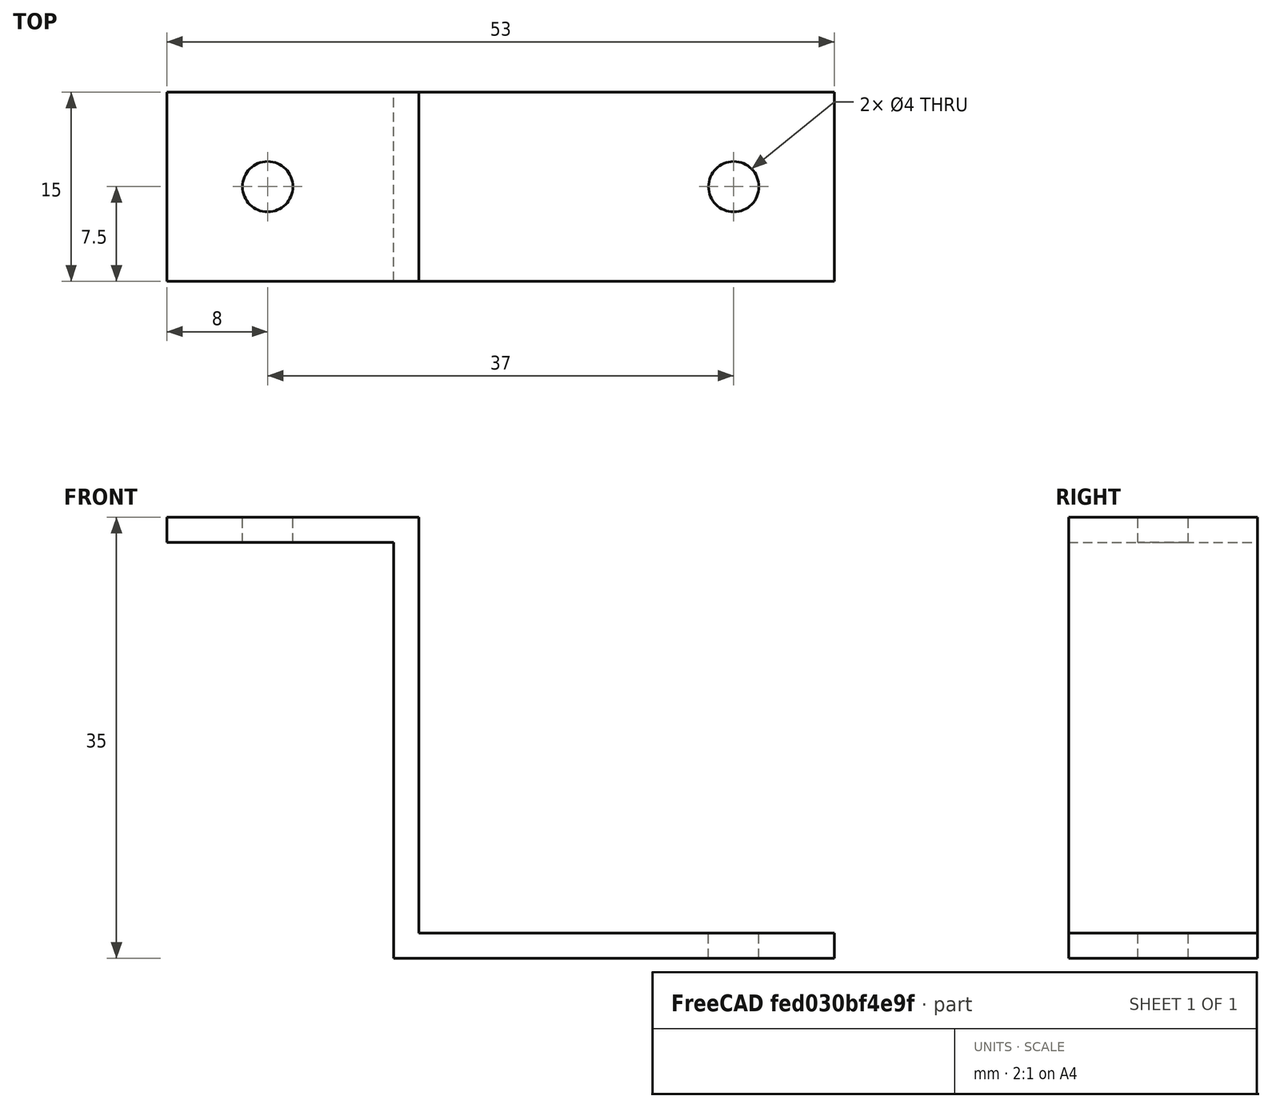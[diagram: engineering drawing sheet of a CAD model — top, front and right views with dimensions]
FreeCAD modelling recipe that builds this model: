
FCSTD DOCUMENT  (FreeCAD 0.18R16131 (Git))
Label: soporteSensorIR
License: All rights reserved
LicenseURL: http://en.wikipedia.org/wiki/All_rights_reserved
objects: Part::Box×3, Part::Cylinder×2, Part::MultiFuse×2, Part::Cut×1
note: 8 computed .brp shape members not serialized (recipe doc carries the construction recipe); baked Part::Feature solids carry a one-line shape summary decoded from their .brp

FEATURE [Part::Box] Box  label="Cubo"
  AttacherType = Attacher::AttachEngine3D
  Height = 2
  Length = 35
  Width = 15
FEATURE [Part::Box] Box001  label="Cubo001"
  AttacherType = Attacher::AttachEngine3D
  Height = 35
  Length = 2
  Width = 15
FEATURE [Part::Box] Box002  label="Cubo002"
  AttacherType = Attacher::AttachEngine3D
  Height = 2
  Length = 20
  Placement = pos=(-18,0,33) rot=(0,0,1;0rad)
  Width = 15
FEATURE [Part::Cylinder] Cylinder  label="Cilindro"
  Angle = 360
  AttacherType = Attacher::AttachEngine3D
  Height = 10
  Placement = pos=(27,7.5,-3) rot=(0,0,1;0rad)
  Radius = 2
FEATURE [Part::Cylinder] Cylinder001  label="Cilindro001"
  Angle = 360
  AttacherType = Attacher::AttachEngine3D
  Height = 10
  Placement = pos=(-10,7.5,29) rot=(0,0,1;0rad)
  Radius = 2
FEATURE [Part::MultiFuse] Fusion
  Shapes = -> [Box,Box002,Box001]
FEATURE [Part::MultiFuse] Fusion001
  Shapes = -> [Cylinder,Cylinder001]
FEATURE [Part::Cut] Cut
  Base = -> Fusion
  Tool = -> Fusion001
